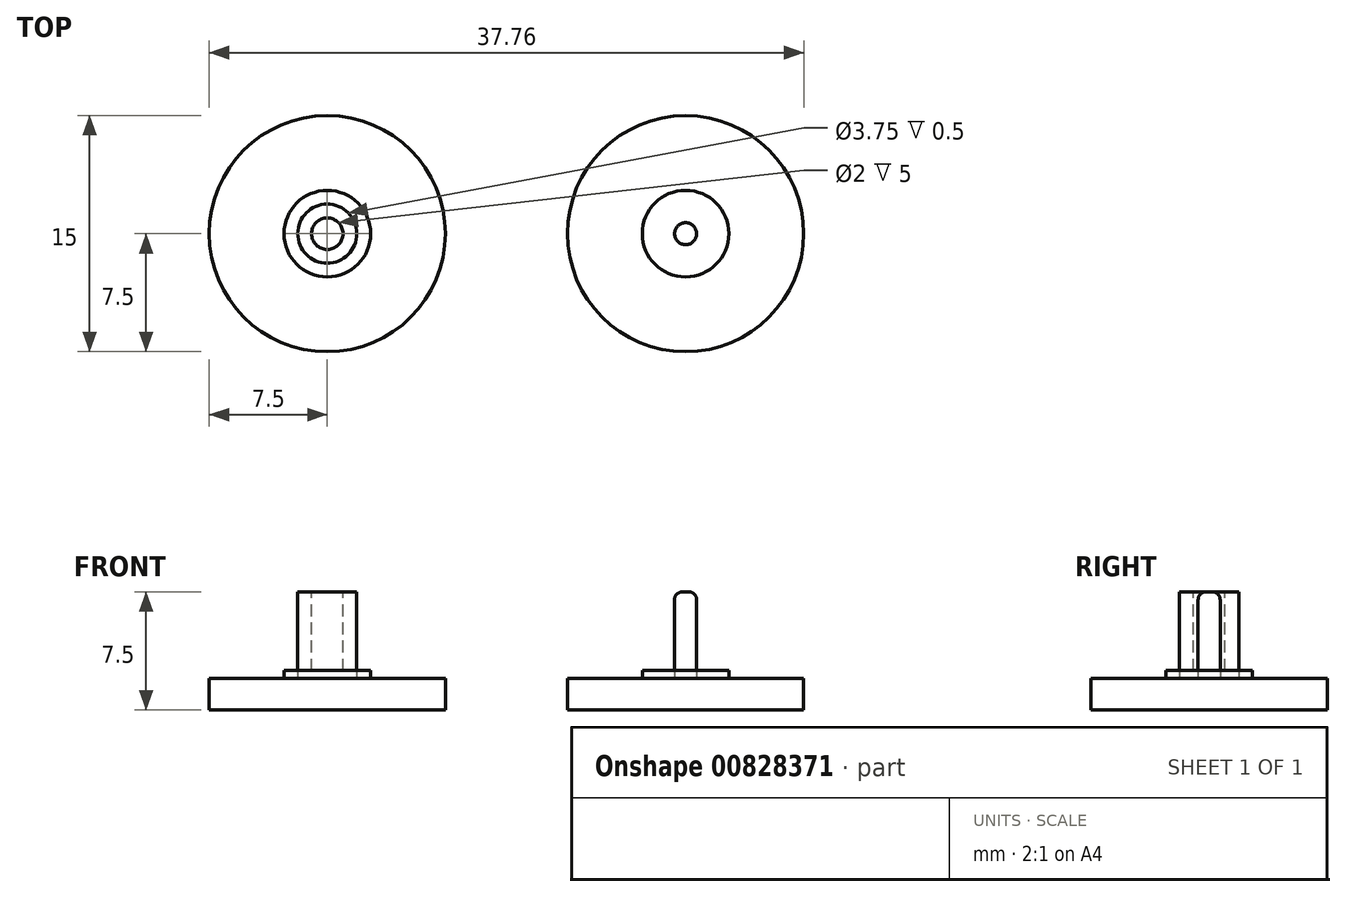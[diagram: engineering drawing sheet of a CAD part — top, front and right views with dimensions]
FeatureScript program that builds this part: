
annotation { "Feature Type Name" : "Feature", "Feature Type Description" : "" }
export const myFeature = defineFeature(function(context is Context, id is Id, definition is map)
    precondition{}
    {
        {
            var Q0;
            Q0=qCreatedBy(makeId("Top.planeOp"),FACE);
            var sketch = newSketch(context, id + "F0", { "sketchPlane" : qUnion([Q0])});
            skCircle(sketch, "E0", {"center": v(0, 0) * mm, "radius": 7.5 * mm});
            skCircle(sketch, "E1", {"center": v(22.76, 0) * mm, "radius": 7.5 * mm});
            skSolve(sketch);
        }
        {
            var Q0;
            Q0 = qSketchRegion(id + "F0", true);
            extrude(context, id + "F1", {"entities" : qUnion([Q0]), "oppositeDirection" : true, "depth" : 2 * mm, "offsetDistance" : 25 * mm});
        }
        {
            var Q0;
            Q0=qCreatedBy(makeId("Top.planeOp"),FACE);
            var sketch = newSketch(context, id + "F2", { "sketchPlane" : qUnion([Q0])});
            skCircle(sketch, "E2", {"center": v(0, 0) * mm, "radius": 1.88 * mm});
            skSolve(sketch);
        }
        {
            var Q0;
            Q0 = qSketchRegion(id + "F2", true);
            extrude(context, id + "F3", {"entities" : qUnion([Q0]), "operationType" : NewBodyOperationType.ADD, "depth" : 5.5 * mm, "offsetDistance" : 25 * mm});
        }
        {
            var Q0;
            Q0=makeQuery(id+"F3.opExtrude","CAP_FACE",FACE,{"disambiguationData":[OSD([sQuery(id+"F2.wireOp",EDGE,"E2")])],"isStart":false});
            var sketch = newSketch(context, id + "F4", { "sketchPlane" : qUnion([Q0])});
            skCircle(sketch, "E3", {"center": v(0, 0) * mm, "radius": 1 * mm});
            skSolve(sketch);
        }
        {
            var Q0;
            Q0 = qSketchRegion(id + "F4", true);
            extrude(context, id + "F5", {"entities" : qUnion([Q0]), "operationType" : NewBodyOperationType.REMOVE, "oppositeDirection" : true, "depth" : 5 * mm, "offsetDistance" : 25 * mm});
        }
        {
            var Q0;
            Q0=makeQuery(id+"F1.opExtrude","CAP_FACE",FACE,{"disambiguationData":[OSD([sQuery(id+"F0.wireOp",EDGE,"E1")])],"isStart":true});
            var sketch = newSketch(context, id + "F6", { "sketchPlane" : qUnion([Q0])});
            skCircle(sketch, "E4", {"center": v(22.76, 0) * mm, "radius": 0.7 * mm});
            skSolve(sketch);
        }
        {
            var Q0;
            Q0 = qSketchRegion(id + "F6", true);
            extrude(context, id + "F7", {"entities" : qUnion([Q0]), "operationType" : NewBodyOperationType.ADD, "depth" : 5.5 * mm, "offsetDistance" : 25 * mm});
        }
        {
            var Q0;
            Q0=makeQuery(id+"F7.opExtrude","CAP_FACE",FACE,{"disambiguationData":[OSD([sQuery(id+"F6.wireOp",EDGE,"E4")])],"isStart":false});
            var Q1;
            Q1=makeQuery(id+"F5.boolean.opBoolean","COPY",EDGE,{"derivedFrom":makeQuery(id+"F5.opExtrude","CAP_EDGE",EDGE,{"disambiguationData":[OSD([sQuery(id+"F4.wireOp",EDGE,"E3")])],"isStart":true})});
            fillet(context, id + "F8", {"entities" : qUnion([Q0, Q1]), "radius" : 0.5 * mm, "tangentPropagation" : true, "allowEdgeOverflow" : false});
        }
        {
            var Q0;
            Q0=qCreatedBy(makeId("Top.planeOp"),FACE);
            cPlane(context, id + "F9", {"entities" : qUnion([Q0]), "cplaneType" : CPlaneType.OFFSET, "offset" : 25 * mm, "oppositeDirection" : true, "width" : 150 * mm, "height" : 150 * mm});
        }
        {
            var Q0;
            Q0=qCreatedBy(id+"F9.planeOp",FACE);
            var sketch = newSketch(context, id + "F10", { "sketchPlane" : qUnion([Q0])});
            skLineSegment(sketch, "E5", {"start": v(0, -32.43) * mm, "end": v(0, 26.07) * mm});
            skLineSegment(sketch, "E6", {"start": v(22.83, 0) * mm, "end": v(22.83, -32.01) * mm});
            skLineSegment(sketch, "E7", {"start": v(22.83, -32.01) * mm, "end": v(22.83, 25.88) * mm});
            skLineSegment(sketch, "E8", {"start": v(22.83, 25.88) * mm, "end": v(22.83, 0) * mm});
            skSolve(sketch);
        }
        {
            var Q0;
            Q0=qCreatedBy(id+"F9.planeOp",FACE);
            var sketch = newSketch(context, id + "F11", { "sketchPlane" : qUnion([Q0])});
            skArc(sketch, "E9", {"start": v(0, -23) * mm, "mid": v(23, 0) * mm, "end": v(0, 23) * mm});
            skLineSegment(sketch, "E10", {"start": v(0, -23) * mm, "end": v(0, 23) * mm});
            skSolve(sketch);
        }
        {
            var Q0;
            Q0 = qSketchRegion(id + "F11", true);
            var Q1;
            Q1=sQuery(id+"F10.wireOp",EDGE,"E5");
            revolve(context, id + "F12", {"operationType" : NewBodyOperationType.REMOVE, "surfaceOperationType" : NewSurfaceOperationType.NEW, "entities" : qUnion([Q0]), "axis" : qUnion([Q1]), "revolveType" : RevolveType.FULL});
        }
        {
            var Q0;
            Q0=qCreatedBy(id+"F9.planeOp",FACE);
            var sketch = newSketch(context, id + "F13", { "sketchPlane" : qUnion([Q0])});
            skArc(sketch, "E11", {"start": v(22.76, -23) * mm, "mid": v(45.76, 0) * mm, "end": v(22.76, 23) * mm});
            skLineSegment(sketch, "E12", {"start": v(22.76, -23) * mm, "end": v(22.76, 23) * mm});
            skSolve(sketch);
        }
        {
            var Q0;
            Q0 = qSketchRegion(id + "F13", true);
            var Q1;
            Q1=sQuery(id+"F13.wireOp",EDGE,"E12");
            revolve(context, id + "F14", {"operationType" : NewBodyOperationType.REMOVE, "surfaceOperationType" : NewSurfaceOperationType.NEW, "entities" : qUnion([Q0]), "axis" : qUnion([Q1]), "revolveType" : RevolveType.FULL});
        }
        {
            var Q0;
            Q0=makeQuery(id+"F1.opExtrude","CAP_FACE",FACE,{"disambiguationData":[OSD([sQuery(id+"F0.wireOp",EDGE,"E0")])],"isStart":true});
            var sketch = newSketch(context, id + "F15", { "sketchPlane" : qUnion([Q0])});
            skCircle(sketch, "E13", {"center": v(0, 0) * mm, "radius": 2.75 * mm});
            skCircle(sketch, "E14", {"center": v(22.76, 0) * mm, "radius": 2.75 * mm});
            skSolve(sketch);
        }
        {
            var Q0;
            Q0=makeQuery(id+"F15.imprint","IMPRINT",FACE,{"disambiguationData":[TD([[makeQuery(id+"F15.imprint","IMPRINT",EDGE,{"derivedFrom":sQuery(id+"F15.wireOp",EDGE,"E13")}),1.0]])]});
            var Q1;
            Q1=makeQuery(id+"F15.imprint","IMPRINT",FACE,{"disambiguationData":[TD([[makeQuery(id+"F15.imprint","IMPRINT",EDGE,{"derivedFrom":sQuery(id+"F15.wireOp",EDGE,"E14")}),1.0]])]});
            var Q2;
            Q2=sQuery(id+"F15.wireOp",EDGE,"E14");
            extrude(context, id + "F16", {"entities" : qUnion([Q0, Q1]), "surfaceEntities" : qUnion([Q2]), "depth" : 0.5 * mm, "offsetDistance" : 25 * mm});
        }
    });
